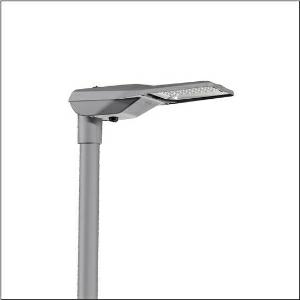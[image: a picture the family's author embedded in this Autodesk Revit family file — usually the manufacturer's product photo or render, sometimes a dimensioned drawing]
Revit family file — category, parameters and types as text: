
# Revit family: streetlight_sl_21_mini___p0_8a_5xe2u33t08jb_ddfb
name_source: partatom
category: Lighting Fixtures
units: mm (PartAtom-declared; Revit-internal decimal feet)

## family parameters
Cut with Voids When Loaded = No
Host = Face
Light Source = No
Part Type = Normal
Room Calculation Point = No
Round Connector Dimension = Use Diameter
Shared = No

## types (1)
- --- (1 x LED, 13050 lm, 88.6 W, 3000K)
    Apparent Load = 89 VA
    CIE Flux Codes = 36 69 97 100 100
    Color Rendering = 70
    Color Temperature = 3000K
    Default Elevation = 1800 mm
    Description = Streetlight SL 21 mini, mast luminaire, primary light control with lens, of PMMA, primary optical cover: cover, of toughened safety glass, transparent, light distribution: P0.8a, light emission: direct distribution, primary light characteristic: asymmetric, installation type: post-top, side-entry, LED, High Power LED, rated luminous flux: 13.050lm, luminous efficacy: 147lm/W, light colour: 730, colour temperature: 3000K, control gear: D4i, control: pre-setting: logarithmic dimming characteristic, flexible luminous flux parameterisation, time-dependent luminous flux control, constant luminous flux control, overheat protection, mains connection: 220..240V, AC, 50/60Hz, start of lifetime: 89W, end of service life: 92W, reduction: 41W, luminaire housing, of diecast aluminium, powder-coated, SITECO metallic grey (DB 702S), corrosivity category C5 high according to DIN EN ISO 12944, multi-level sealing system, sealing non-destructively replaceable, inclination adjustable: 0°, 5°, 10°, 15°, please order mast flange separately, length: 628mm, width: 235mm, height: 110mm, mast flange for spigot size: 42mm (side-entry): 5XC10008XM4, 60/48mm (side-entry/post-top): 5XC10108XM2, 76/60mm (side-entry/post-top): 5XC10108XM1, mounting height: 4..8m, Smart Interface below and above, protection rating (complete): IP66, insulation class (complete): insulation class II (safety insulation), certification: CE, ENEC, ENEC+, VDE, impact resistance: IK10, permissible operating ambient temperature for outdoor applications: -40..+50°C, standard-compliant lighting for roads and squares, packaging unit: 1 piece

Light Distribution: P0.8a
    Height = 110 mm
    Lamp = 1 x LED
    Lamp Light Flux = 13050 lm
    Lamp Power = 88.6 W
    Lamp count = 1
    Length = 625 mm
    Luminous efficacy = 147 lm/W
    Manufacturer = Siteco
    ModVariant = No
    Model = 5XE2U33T08JB
    Number of Poles = 1
    OnlyDefault = Yes
    Power Factor = 1
    Product Name = Streetlight SL 21 mini | P0.8a
    Product group = mast luminaire | pylon top
    ProductGroupID = 6100
    Protection Class = Protection class II
    Protection Degree = IP 66
    RLX_Detail_Level = 1
    RLX_Emergency_Light_Flux = 0 lm
    RLX_Emergency_Type = 0
    RLX_Emergency_Type_DB = No
    RlxData = <blob elided: 26253 chars, md5=368b154a>
    Socket = socket
    Standby Power = 0 W
    System Light Flux = 13050 lm
    System Power = 89 W
    Type Comments = factory setting: luminous flux: 100 % | dim-lin: 254 | 915 mA
    Type Image = l_1003514.jpg
    URL = http://relux.com
    VarID = @adj_033039
    Voltage = 0 V
    Weight = 0.00 kg
    Width = 234 mm

## geometry (parser evidence)
native form markers: Blend x4, Sweep x12
no freeform markers — native parametric forms only
